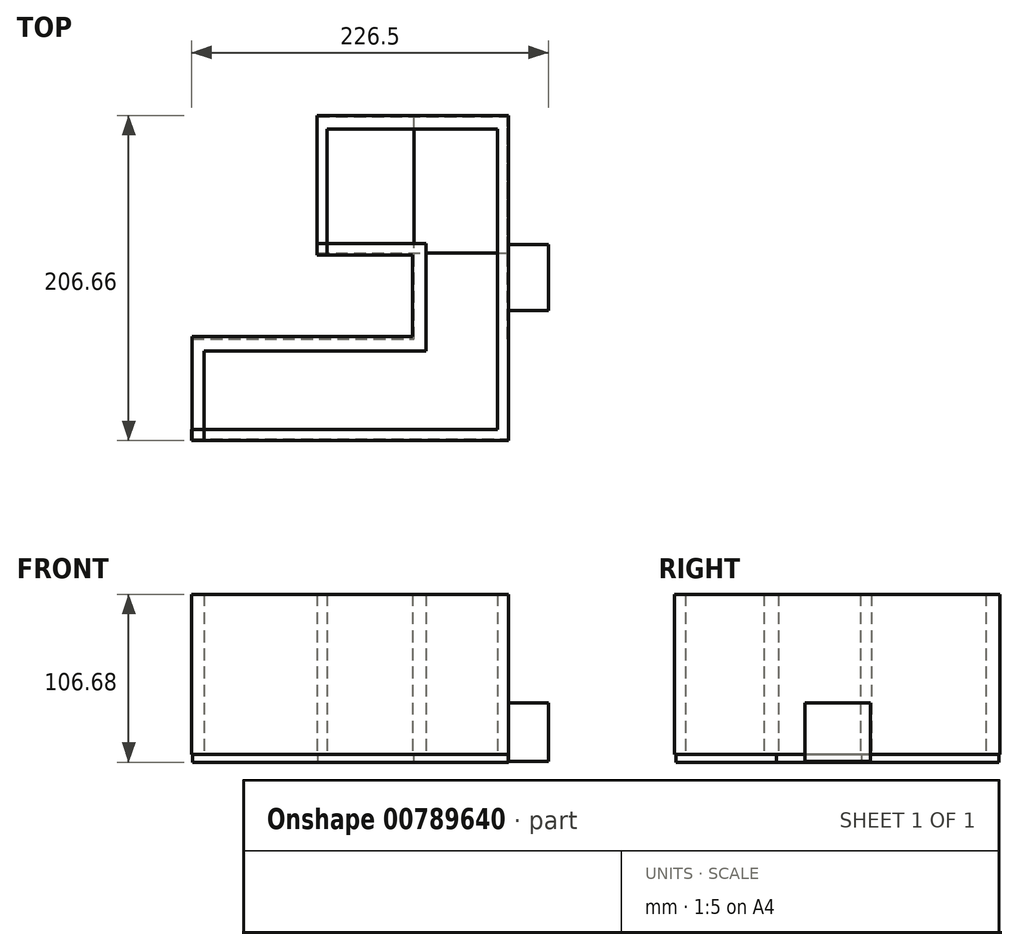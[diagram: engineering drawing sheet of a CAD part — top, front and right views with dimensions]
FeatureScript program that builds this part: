
annotation { "Feature Type Name" : "Feature", "Feature Type Description" : "" }
export const myFeature = defineFeature(function(context is Context, id is Id, definition is map)
    precondition{}
    {
        {
            var Q0;
            Q0=qCreatedBy(makeId("Top.planeOp"),FACE);
            var sketch = newSketch(context, id + "F0", { "sketchPlane" : qUnion([Q0])});
            skLineSegment(sketch, "E0.bottom", {"start": v(-96.68, -97.5) * mm, "end": v(97.5, -97.5) * mm});
            skLineSegment(sketch, "E0.top", {"start": v(-96.68, -104.48) * mm, "end": v(97.5, -104.48) * mm});
            skLineSegment(sketch, "E0.left", {"start": v(-96.68, -97.5) * mm, "end": v(-96.68, -104.48) * mm});
            skLineSegment(sketch, "E0.right", {"start": v(97.5, -97.5) * mm, "end": v(97.5, -104.48) * mm});
            skLineSegment(sketch, "E1.bottom", {"start": v(97.5, -104.48) * mm, "end": v(104.42, -104.48) * mm});
            skLineSegment(sketch, "E1.top", {"start": v(97.5, 102.18) * mm, "end": v(104.42, 102.18) * mm});
            skLineSegment(sketch, "E1.left", {"start": v(97.5, -104.48) * mm, "end": v(97.5, 102.18) * mm});
            skLineSegment(sketch, "E1.right", {"start": v(104.42, -104.48) * mm, "end": v(104.42, 102.18) * mm});
            skLineSegment(sketch, "E2.bottom", {"start": v(104.42, 102.18) * mm, "end": v(-10.83, 102.18) * mm});
            skLineSegment(sketch, "E2.top", {"start": v(104.42, 93.5) * mm, "end": v(-10.83, 93.5) * mm});
            skLineSegment(sketch, "E2.left", {"start": v(104.42, 102.18) * mm, "end": v(104.42, 93.5) * mm});
            skLineSegment(sketch, "E2.right", {"start": v(-10.83, 102.18) * mm, "end": v(-10.83, 93.5) * mm});
            skLineSegment(sketch, "E3.bottom", {"start": v(-17.24, 102.18) * mm, "end": v(-10.83, 102.18) * mm});
            skLineSegment(sketch, "E3.top", {"start": v(-17.24, 13.6) * mm, "end": v(-10.83, 13.6) * mm});
            skLineSegment(sketch, "E3.left", {"start": v(-10.83, 102.18) * mm, "end": v(-10.83, 13.6) * mm});
            skLineSegment(sketch, "E3.right", {"start": v(-17.24, 102.18) * mm, "end": v(-17.24, 13.6) * mm});
            skSolve(sketch);
        }
        {
            var Q0;
            Q0=qCreatedBy(makeId("Top.planeOp"),FACE);
            var sketch = newSketch(context, id + "F1", { "sketchPlane" : qUnion([Q0])});
            skLineSegment(sketch, "E4.bottom", {"start": v(-16.98, 13.6) * mm, "end": v(104.07, 13.6) * mm});
            skLineSegment(sketch, "E4.top", {"start": v(-16.98, 20.72) * mm, "end": v(104.07, 20.72) * mm});
            skLineSegment(sketch, "E4.left", {"start": v(-16.98, 13.6) * mm, "end": v(-16.98, 20.72) * mm});
            skLineSegment(sketch, "E4.right", {"start": v(104.07, 13.6) * mm, "end": v(104.07, 20.72) * mm});
            skLineSegment(sketch, "E5.bottom", {"start": v(-96.58, -104.4) * mm, "end": v(-88.95, -104.4) * mm});
            skLineSegment(sketch, "E5.top", {"start": v(-96.58, -38.28) * mm, "end": v(-88.95, -38.28) * mm});
            skLineSegment(sketch, "E5.left", {"start": v(-96.58, -104.4) * mm, "end": v(-96.58, -38.28) * mm});
            skLineSegment(sketch, "E5.right", {"start": v(-88.95, -104.4) * mm, "end": v(-88.95, -38.28) * mm});
            skLineSegment(sketch, "E6.bottom", {"start": v(-96.58, -38.28) * mm, "end": v(104.35, -38.28) * mm});
            skLineSegment(sketch, "E6.top", {"start": v(-96.58, -47.55) * mm, "end": v(104.35, -47.55) * mm});
            skLineSegment(sketch, "E6.left", {"start": v(-96.58, -38.28) * mm, "end": v(-96.58, -47.55) * mm});
            skLineSegment(sketch, "E6.right", {"start": v(104.35, -38.28) * mm, "end": v(104.35, -47.55) * mm});
            skLineSegment(sketch, "E7.bottom", {"start": v(43.54, 20.72) * mm, "end": v(52.06, 20.72) * mm});
            skLineSegment(sketch, "E7.top", {"start": v(43.54, -47.55) * mm, "end": v(52.06, -47.55) * mm});
            skLineSegment(sketch, "E7.left", {"start": v(43.54, 20.72) * mm, "end": v(43.54, -47.55) * mm});
            skLineSegment(sketch, "E7.right", {"start": v(52.06, 20.72) * mm, "end": v(52.06, -47.55) * mm});
            skSolve(sketch);
        }
        {
            var Q0;
            {var subQ0=sQuery(id+"F0.wireOp",EDGE,"E1.top");Q0=makeQuery(id+"F0.imprint","IMPRINT",FACE,{"disambiguationData":[TD([[makeQuery(id+"F0.imprint","IMPRINT",EDGE,{"derivedFrom":subQ0}),-1.0]])]});}
            var Q1;
            {var subQ0=sQuery(id+"F1.wireOp",EDGE,"E5.bottom");Q1=makeQuery(id+"F1.imprint","IMPRINT",FACE,{"disambiguationData":[TD([[makeQuery(id+"F1.imprint","IMPRINT",EDGE,{"derivedFrom":subQ0}),1.0]])]});}
            var Q2;
            {var subQ1=sQuery(id+"F0.wireOp",EDGE,"E0.right");Q2=makeQuery(id+"F0.imprint","IMPRINT",FACE,{"disambiguationData":[TD([[makeQuery(id+"F0.imprint","IMPRINT",EDGE,{"derivedFrom":subQ1}),1.0]])]});}
            var Q3;
            Q3=makeQuery(id+"F0.imprint","IMPRINT",FACE,{"disambiguationData":[TD([[makeQuery(id+"F0.imprint","IMPRINT",EDGE,{"derivedFrom":sQuery(id+"F0.wireOp",EDGE,"E0.bottom")}),-1.0]])]});
            var Q4;
            {var subQ1=sQuery(id+"F1.wireOp",EDGE,"E5.right");var subQ3=sQuery(id+"F1.wireOp",EDGE,"E6.top");var subQ4=makeQuery(id+"F1.imprint","INTERSECT",VERTEX,{"derivedFrom":[subQ1,subQ3]});Q4=makeQuery(id+"F1.imprint","IMPRINT",FACE,{"disambiguationData":[TD([[makeQuery(id+"F1.imprint","IMPRINT",EDGE,{"disambiguationData":[TD([[subQ4,-1.0]])],"derivedFrom":subQ3}),1.0]])]});}
            var Q5;
            {var subQ0=sQuery(id+"F1.wireOp",EDGE,"E5.top");Q5=makeQuery(id+"F1.imprint","IMPRINT",FACE,{"disambiguationData":[TD([[makeQuery(id+"F1.imprint","IMPRINT",EDGE,{"derivedFrom":subQ0}),-1.0]])]});}
            var Q6;
            Q6=makeQuery(id+"F0.imprint","IMPRINT",FACE,{"disambiguationData":[TD([[makeQuery(id+"F0.imprint","IMPRINT",EDGE,{"derivedFrom":sQuery(id+"F0.wireOp",EDGE,"E2.right")}),-1.0]])]});
            var Q7;
            {var subQ0=sQuery(id+"F1.wireOp",EDGE,"E7.right");var subQ1=sQuery(id+"F1.wireOp",EDGE,"E4.bottom");var subQ2=makeQuery(id+"F1.imprint","INTERSECT",VERTEX,{"derivedFrom":[subQ1,subQ0]});Q7=makeQuery(id+"F1.imprint","IMPRINT",FACE,{"disambiguationData":[TD([[makeQuery(id+"F1.imprint","IMPRINT",EDGE,{"disambiguationData":[TD([[subQ2,1.0]])],"derivedFrom":subQ1}),-1.0]])]});}
            var Q8;
            {var subQ0=sQuery(id+"F1.wireOp",EDGE,"E7.right");var subQ1=sQuery(id+"F1.wireOp",EDGE,"E6.bottom");var subQ2=makeQuery(id+"F1.imprint","INTERSECT",VERTEX,{"derivedFrom":[subQ1,subQ0]});Q8=makeQuery(id+"F1.imprint","IMPRINT",FACE,{"disambiguationData":[TD([[makeQuery(id+"F1.imprint","IMPRINT",EDGE,{"disambiguationData":[TD([[subQ2,1.0]])],"derivedFrom":subQ1}),-1.0]])]});}
            var Q9;
            {var subQ0=sQuery(id+"F0.wireOp",EDGE,"E2.bottom");Q9=makeQuery(id+"F0.imprint","IMPRINT",FACE,{"disambiguationData":[TD([[makeQuery(id+"F0.imprint","IMPRINT",EDGE,{"derivedFrom":subQ0}),1.0]])]});}
            var Q10;
            {var subQ0=sQuery(id+"F0.wireOp",EDGE,"E2.bottom");var subQ2=sQuery(id+"F0.wireOp",EDGE,"E1.top");var subQ7=sQuery(id+"F0.wireOp",EDGE,"E2.right");var subQ8=makeQuery(id+"F0.imprint","IMPRINT",EDGE,{"derivedFrom":subQ7});var subQ12=sQuery(id+"F0.wireOp",EDGE,"E0.right");var subQ13=sQuery(id+"F0.wireOp",EDGE,"E0.bottom");var subQ15=makeQuery(id+"F0.imprint","IMPRINT",EDGE,{"derivedFrom":subQ12});Q10=qUnion([makeQuery(id+"F0.imprint","IMPRINT",FACE,{"disambiguationData":[TD([[makeQuery(id+"F0.imprint","IMPRINT",EDGE,{"derivedFrom":subQ13}),-1.0]])]}),makeQuery(id+"F0.imprint","IMPRINT",FACE,{"disambiguationData":[TD([[subQ8,-1.0]])]}),makeQuery(id+"F0.imprint","IMPRINT",FACE,{"disambiguationData":[TD([[subQ15,1.0]])]}),makeQuery(id+"F0.imprint","IMPRINT",FACE,{"disambiguationData":[TD([[makeQuery(id+"F0.imprint","IMPRINT",EDGE,{"derivedFrom":subQ2}),-1.0]])]}),makeQuery(id+"F0.imprint","IMPRINT",FACE,{"disambiguationData":[TD([[makeQuery(id+"F0.imprint","IMPRINT",EDGE,{"derivedFrom":subQ0}),1.0]])]})]);}
            var Q11;
            {var subQ0=sQuery(id+"F1.wireOp",EDGE,"E4.left");Q11=makeQuery(id+"F1.imprint","IMPRINT",FACE,{"disambiguationData":[TD([[makeQuery(id+"F1.imprint","IMPRINT",EDGE,{"derivedFrom":subQ0}),-1.0]])]});}
            var Q12;
            {var subQ0=sQuery(id+"F1.wireOp",EDGE,"E7.right");var subQ1=sQuery(id+"F1.wireOp",EDGE,"E4.bottom");var subQ2=makeQuery(id+"F1.imprint","INTERSECT",VERTEX,{"derivedFrom":[subQ1,subQ0]});Q12=makeQuery(id+"F1.imprint","IMPRINT",FACE,{"disambiguationData":[TD([[makeQuery(id+"F1.imprint","IMPRINT",EDGE,{"disambiguationData":[TD([[subQ2,1.0]])],"derivedFrom":subQ1}),1.0]])]});}
            extrude(context, id + "F2", {"entities" : qUnion([Q0, Q1, Q2, Q3, Q4, Q5, Q6, Q7, Q8, Q9, Q10, Q11, Q12]), "depth" : 101.6 * mm, "offsetDistance" : 25.4 * mm});
        }
        {
            var Q0;
            Q0=qCreatedBy(makeId("Top.planeOp"),FACE);
            var sketch = newSketch(context, id + "F3", { "sketchPlane" : qUnion([Q0])});
            skLineSegment(sketch, "E8.bottom", {"start": v(-96.24, -103.39) * mm, "end": v(104.5, -103.39) * mm});
            skLineSegment(sketch, "E8.top", {"start": v(-96.24, -39.76) * mm, "end": v(104.5, -39.76) * mm});
            skLineSegment(sketch, "E8.left", {"start": v(-96.24, -103.39) * mm, "end": v(-96.24, -39.76) * mm});
            skLineSegment(sketch, "E8.right", {"start": v(104.5, -103.39) * mm, "end": v(104.5, -39.76) * mm});
            skLineSegment(sketch, "E9.bottom", {"start": v(44.37, -39.76) * mm, "end": v(103.9, -39.76) * mm});
            skLineSegment(sketch, "E9.top", {"start": v(44.37, 101.72) * mm, "end": v(103.9, 101.72) * mm});
            skLineSegment(sketch, "E9.left", {"start": v(44.37, -39.76) * mm, "end": v(44.37, 101.72) * mm});
            skLineSegment(sketch, "E9.right", {"start": v(103.9, -39.76) * mm, "end": v(103.9, 101.72) * mm});
            skSolve(sketch);
        }
        {
            var Q0;
            Q0=qCreatedBy(makeId("Top.planeOp"),FACE);
            var sketch = newSketch(context, id + "F4", { "sketchPlane" : qUnion([Q0])});
            skLineSegment(sketch, "E10.bottom", {"start": v(-16.56, 14.61) * mm, "end": v(103.88, 14.61) * mm});
            skLineSegment(sketch, "E10.top", {"start": v(-16.56, 101.45) * mm, "end": v(103.88, 101.45) * mm});
            skLineSegment(sketch, "E10.left", {"start": v(-16.56, 14.61) * mm, "end": v(-16.56, 101.45) * mm});
            skLineSegment(sketch, "E10.right", {"start": v(103.88, 14.61) * mm, "end": v(103.88, 101.45) * mm});
            skSolve(sketch);
        }
        {
            var Q0;
            Q0=makeQuery(id+"F3.imprint","IMPRINT",FACE,{"disambiguationData":[TD([[makeQuery(id+"F3.imprint","IMPRINT",EDGE,{"derivedFrom":sQuery(id+"F3.wireOp",EDGE,"E9.top")}),-1.0]])]});
            var Q1;
            Q1=makeQuery(id+"F4.imprint","IMPRINT",FACE,{"disambiguationData":[TD([[makeQuery(id+"F4.imprint","IMPRINT",EDGE,{"derivedFrom":sQuery(id+"F4.wireOp",EDGE,"E10.bottom")}),1.0]])]});
            var Q2;
            Q2=makeQuery(id+"F3.imprint","IMPRINT",FACE,{"disambiguationData":[TD([[makeQuery(id+"F3.imprint","IMPRINT",EDGE,{"derivedFrom":sQuery(id+"F3.wireOp",EDGE,"E8.bottom")}),1.0]])]});
            extrude(context, id + "F5", {"entities" : qUnion([Q0, Q1, Q2]), "oppositeDirection" : true, "depth" : 5.08 * mm, "offsetDistance" : 25.4 * mm});
        }
        {
            var Q0;
            Q0=makeQuery(id+"F2.opExtrude","SWEPT_FACE",FACE,{"disambiguationData":[OSD([sQuery(id+"F0.wireOp",EDGE,"E1.right")])]});
            var sketch = newSketch(context, id + "F6", { "sketchPlane" : qUnion([Q0])});
            skLineSegment(sketch, "E11.bottom", {"start": v(-21.67, -4.67) * mm, "end": v(20.15, -4.67) * mm});
            skLineSegment(sketch, "E11.top", {"start": v(-21.67, 32.6) * mm, "end": v(20.15, 32.6) * mm});
            skLineSegment(sketch, "E11.left", {"start": v(-21.67, -4.67) * mm, "end": v(-21.67, 32.6) * mm});
            skLineSegment(sketch, "E11.right", {"start": v(20.15, -4.67) * mm, "end": v(20.15, 32.6) * mm});
            skSolve(sketch);
        }
        {
            var Q0;
            {var subQ0=sQuery(id+"F6.wireOp",EDGE,"E11.bottom");Q0=makeQuery(id+"F6.imprint","IMPRINT",FACE,{"disambiguationData":[TD([[makeQuery(id+"F6.imprint","IMPRINT",EDGE,{"derivedFrom":subQ0}),1.0]])]});}
            var Q1;
            {var subQ0=sQuery(id+"F6.wireOp",EDGE,"E11.top");Q1=makeQuery(id+"F6.imprint","IMPRINT",FACE,{"disambiguationData":[TD([[makeQuery(id+"F6.imprint","IMPRINT",EDGE,{"derivedFrom":subQ0}),-1.0]])]});}
            extrude(context, id + "F7", {"entities" : qUnion([Q0, Q1]), "operationType" : NewBodyOperationType.ADD, "depth" : 25.4 * mm, "offsetDistance" : 25.4 * mm});
        }
    });
